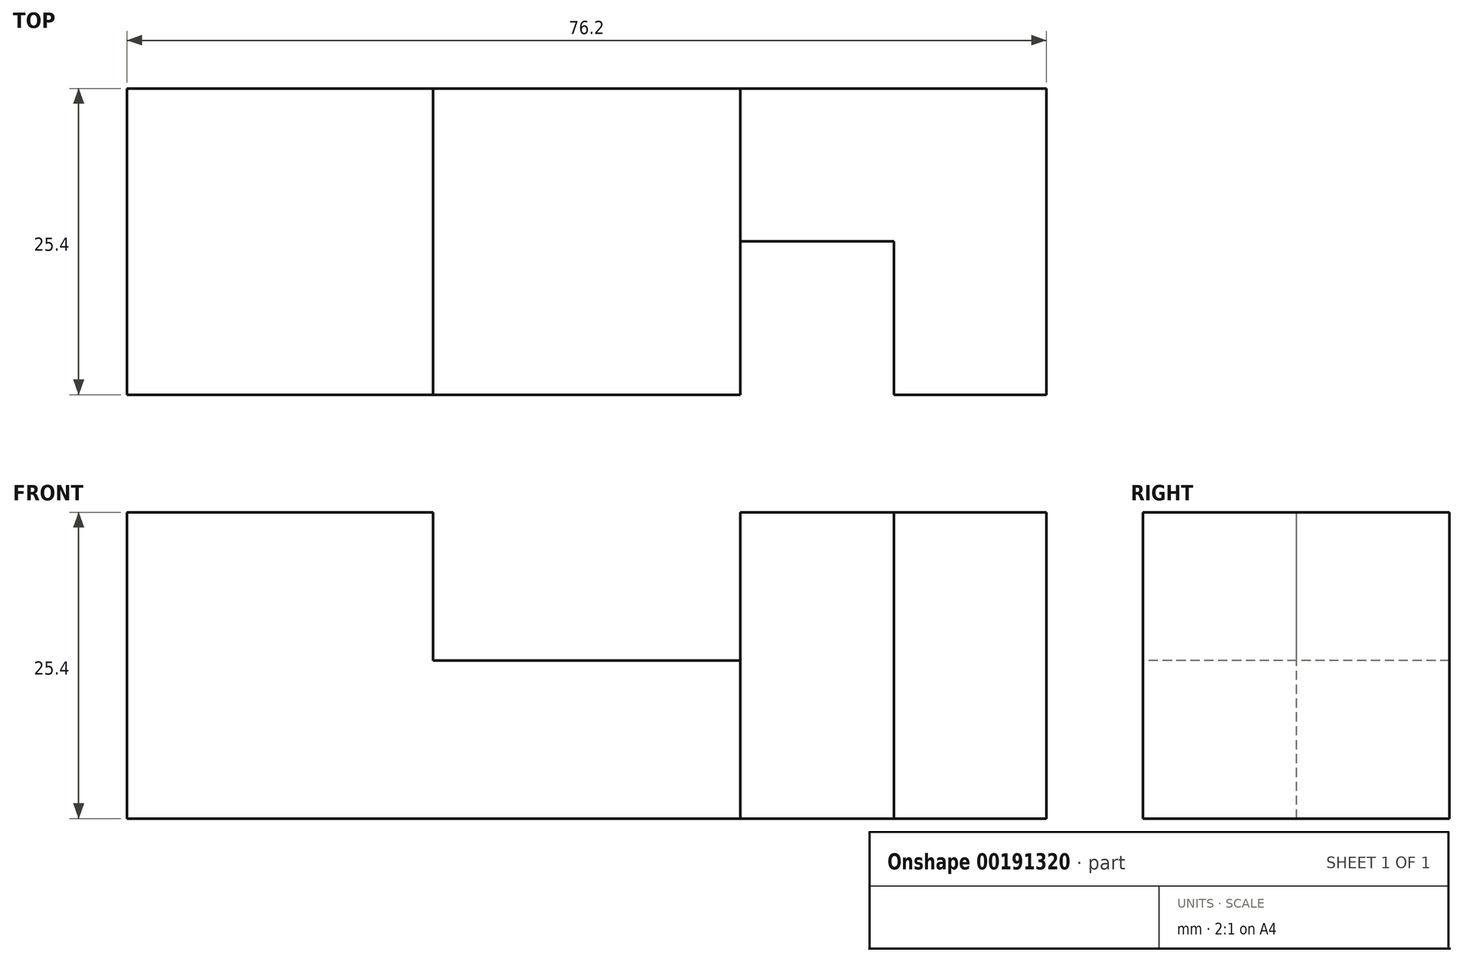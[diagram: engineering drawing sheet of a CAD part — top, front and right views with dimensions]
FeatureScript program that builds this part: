
annotation { "Feature Type Name" : "Feature", "Feature Type Description" : "" }
export const myFeature = defineFeature(function(context is Context, id is Id, definition is map)
    precondition{}
    {
        {
            var Q0;
            Q0=qCreatedBy(makeId("Top.planeOp"),FACE);
            var sketch = newSketch(context, id + "F0", { "sketchPlane" : qUnion([Q0])});
            skLineSegment(sketch, "E0.bottom", {"start": v(0, 0) * mm, "end": v(76.2, 0) * mm});
            skLineSegment(sketch, "E0.top", {"start": v(0, 25.4) * mm, "end": v(76.2, 25.4) * mm});
            skLineSegment(sketch, "E0.left", {"start": v(0, 0) * mm, "end": v(0, 25.4) * mm});
            skLineSegment(sketch, "E0.right", {"start": v(76.2, 0) * mm, "end": v(76.2, 25.4) * mm});
            skSolve(sketch);
        }
        {
            var Q0;
            Q0=makeQuery(id+"F0.imprint","IMPRINT",FACE,{"disambiguationData":[TD([[makeQuery(id+"F0.imprint","IMPRINT",EDGE,{"derivedFrom":sQuery(id+"F0.wireOp",EDGE,"E0.bottom")}),1.0]])]});
            extrude(context, id + "F1", {"entities" : qUnion([Q0]), "depth" : 25.4 * mm});
        }
        {
            var Q0;
            Q0=qCreatedBy(makeId("Front.planeOp"),FACE);
            var sketch = newSketch(context, id + "F2", { "sketchPlane" : qUnion([Q0])});
            skLineSegment(sketch, "E1.bottom", {"start": v(25.37, 25.82) * mm, "end": v(50.83, 25.82) * mm});
            skLineSegment(sketch, "E1.top", {"start": v(25.37, 13.1) * mm, "end": v(50.83, 13.1) * mm});
            skLineSegment(sketch, "E1.left", {"start": v(25.37, 25.82) * mm, "end": v(25.37, 13.1) * mm});
            skLineSegment(sketch, "E1.right", {"start": v(50.83, 25.82) * mm, "end": v(50.83, 13.1) * mm});
            skSolve(sketch);
        }
        {
            var Q0;
            Q0=makeQuery(id+"F2.imprint","IMPRINT",FACE,{"disambiguationData":[TD([[makeQuery(id+"F2.imprint","IMPRINT",EDGE,{"derivedFrom":sQuery(id+"F2.wireOp",EDGE,"E1.bottom")}),-1.0]])]});
            extrude(context, id + "F3", {"entities" : qUnion([Q0]), "operationType" : NewBodyOperationType.REMOVE, "oppositeDirection" : true, "depth" : 25.4 * mm});
        }
        {
            var Q0;
            {var subQ0=sQuery(id+"F0.wireOp",EDGE,"E0.bottom");var subQ1=sQuery(id+"F0.wireOp",EDGE,"E0.top");var subQ2=sQuery(id+"F0.wireOp",EDGE,"E0.right");Q0=makeQuery(id+"F3.boolean.opBoolean","SPLIT",FACE,{"disambiguationData":[TD([makeQuery(id+"F1.opExtrude","SWEPT_FACE",FACE,{"disambiguationData":[OSD([subQ2])]})])],"derivedFrom":makeQuery(id+"F1.opExtrude","CAP_FACE",FACE,{"disambiguationData":[OSD([subQ0,subQ1,sQuery(id+"F0.wireOp",EDGE,"E0.left"),subQ2])],"isStart":false})});}
            var sketch = newSketch(context, id + "F4", { "sketchPlane" : qUnion([Q0])});
            skLineSegment(sketch, "E2.bottom", {"start": v(50.83, 0) * mm, "end": v(63.55, 0) * mm});
            skLineSegment(sketch, "E2.top", {"start": v(50.83, 12.73) * mm, "end": v(63.55, 12.73) * mm});
            skLineSegment(sketch, "E2.left", {"start": v(50.83, 0) * mm, "end": v(50.83, 12.73) * mm});
            skLineSegment(sketch, "E2.right", {"start": v(63.55, 0) * mm, "end": v(63.55, 12.73) * mm});
            skSolve(sketch);
        }
        {
            var Q0;
            Q0=makeQuery(id+"F4.imprint","IMPRINT",FACE,{"disambiguationData":[TD([[makeQuery(id+"F4.imprint","IMPRINT",EDGE,{"derivedFrom":sQuery(id+"F4.wireOp",EDGE,"E2.bottom")}),1.0]])]});
            extrude(context, id + "F5", {"entities" : qUnion([Q0]), "operationType" : NewBodyOperationType.REMOVE, "oppositeDirection" : true, "depth" : 25.4 * mm});
        }
    });
